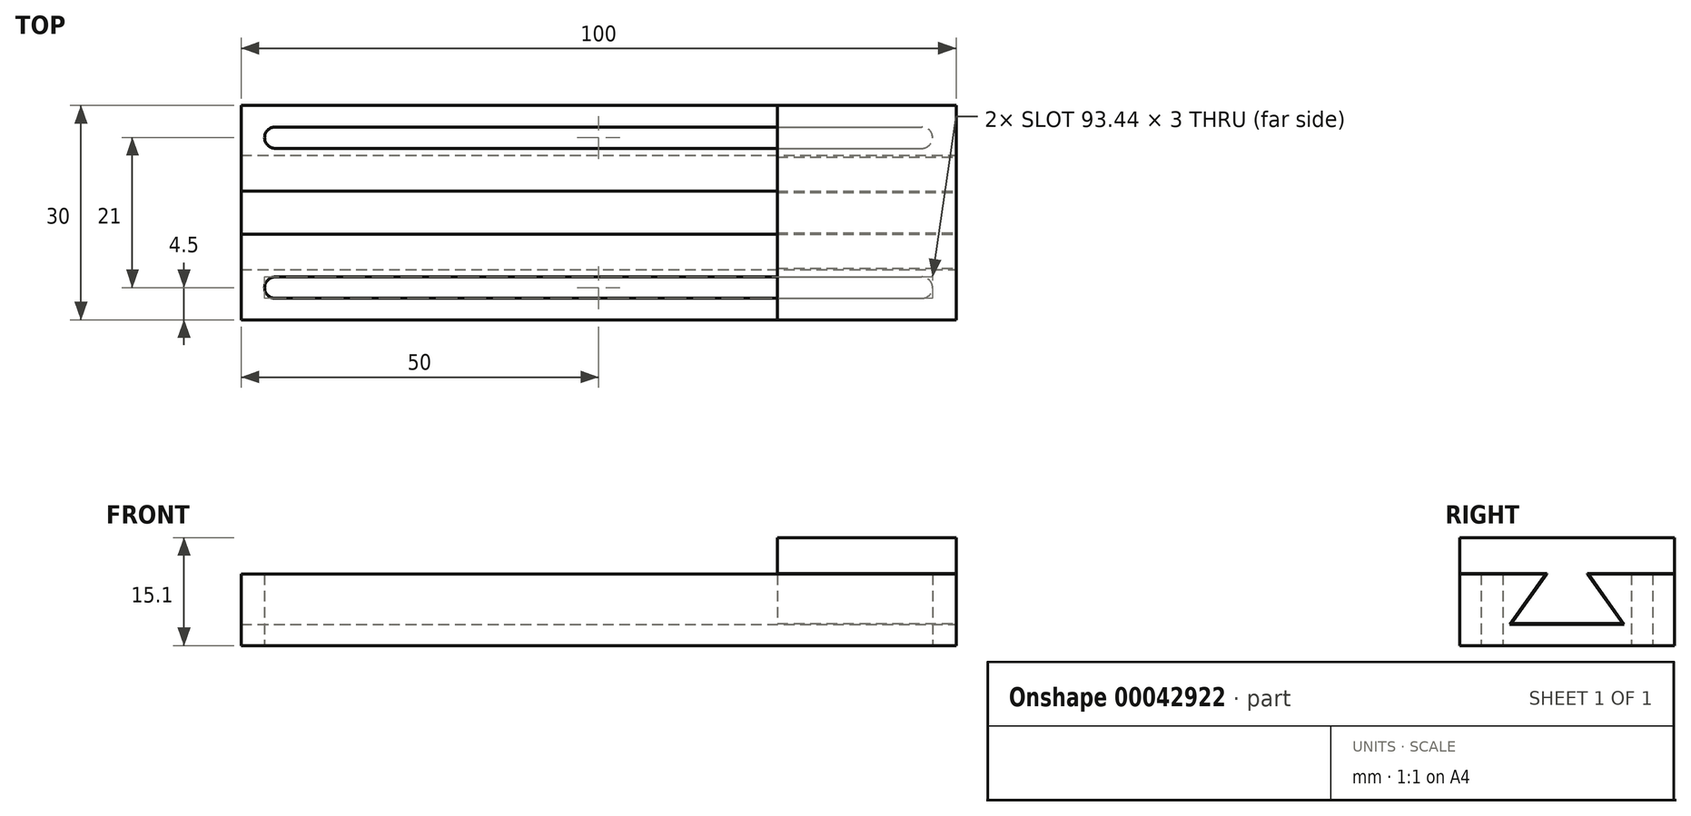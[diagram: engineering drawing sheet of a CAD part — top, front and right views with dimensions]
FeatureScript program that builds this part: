
annotation { "Feature Type Name" : "Feature", "Feature Type Description" : "" }
export const myFeature = defineFeature(function(context is Context, id is Id, definition is map)
    precondition{}
    {
        {
            var Q0;
            Q0=qCreatedBy(makeId("Top.planeOp"),FACE);
            var sketch = newSketch(context, id + "F0", { "sketchPlane" : qUnion([Q0])});
            skLineSegment(sketch, "E0.bottom", {"start": v(-50, 15) * mm, "end": v(50, 15) * mm});
            skLineSegment(sketch, "E0.top", {"start": v(-50, -15) * mm, "end": v(50, -15) * mm});
            skLineSegment(sketch, "E0.left", {"start": v(-50, 15) * mm, "end": v(-50, -15) * mm});
            skLineSegment(sketch, "E0.right", {"start": v(50, 15) * mm, "end": v(50, -15) * mm});
            skLineSegment(sketch, "E1", {"start": v(0, 15) * mm, "end": v(0, -15) * mm, "construction": true});
            skLineSegment(sketch, "E2", {"start": v(-50, 0) * mm, "end": v(50, 0) * mm, "construction": true});
            skLineSegment(sketch, "E3", {"start": v(-50, 3) * mm, "end": v(50, 3) * mm});
            skLineSegment(sketch, "E4", {"start": v(-50, -3) * mm, "end": v(50, -3) * mm});
            skLineSegment(sketch, "E5", {"start": v(-50, 6) * mm, "end": v(50, 6) * mm});
            skLineSegment(sketch, "E6", {"start": v(50, 6) * mm, "end": v(50, -6) * mm});
            skLineSegment(sketch, "E7", {"start": v(50, -6) * mm, "end": v(-50, -6) * mm});
            skLineSegment(sketch, "E8.bottom", {"start": v(-45.22, -9) * mm, "end": v(45.22, -9) * mm});
            skLineSegment(sketch, "E8.top", {"start": v(-45.22, -12) * mm, "end": v(45.22, -12) * mm});
            skLineSegment(sketch, "E8.left", {"start": v(-45.22, -9) * mm, "end": v(-45.22, -12) * mm});
            skLineSegment(sketch, "E8.right", {"start": v(45.22, -9) * mm, "end": v(45.22, -12) * mm});
            skLineSegment(sketch, "E9.bottom", {"start": v(-45.22, 12) * mm, "end": v(45.22, 12) * mm});
            skLineSegment(sketch, "E9.top", {"start": v(-45.22, 9) * mm, "end": v(45.22, 9) * mm});
            skLineSegment(sketch, "E9.left", {"start": v(-45.22, 12) * mm, "end": v(-45.22, 9) * mm});
            skLineSegment(sketch, "E9.right", {"start": v(45.22, 12) * mm, "end": v(45.22, 9) * mm});
            skLineSegment(sketch, "E10", {"start": v(0, -12) * mm, "end": v(0, -15) * mm, "construction": true});
            skLineSegment(sketch, "E11", {"start": v(0, 15) * mm, "end": v(0, 12) * mm, "construction": true});
            skLineSegment(sketch, "E12", {"start": v(0, -6) * mm, "end": v(0, -15) * mm, "construction": true});
            skLineSegment(sketch, "E13", {"start": v(0, 15) * mm, "end": v(0, 6) * mm, "construction": true});
            skPoint(sketch, "E14", {"position": v(0, 10.5) * mm});
            skPoint(sketch, "E15", {"position": v(-45.22, 10.5) * mm});
            skPoint(sketch, "E16", {"position": v(-45.22, -10.5) * mm});
            skPoint(sketch, "E17", {"position": v(45.22, -10.5) * mm});
            skPoint(sketch, "E18", {"position": v(45.22, 10.5) * mm});
            skLineSegment(sketch, "E19", {"start": v(-50, 72.94) * mm, "end": v(-50, -39.34) * mm, "construction": true});
            skLineSegment(sketch, "E20", {"start": v(0, -31.19) * mm, "end": v(0, 115.5) * mm, "construction": true});
            skSolve(sketch);
        }
        {
            var Q0;
            {var subQ0=sQuery(id+"F0.wireOp",EDGE,"E0.bottom");Q0=makeQuery(id+"F0.imprint","IMPRINT",FACE,{"disambiguationData":[TD([[makeQuery(id+"F0.imprint","IMPRINT",EDGE,{"derivedFrom":subQ0}),-1.0]])]});}
            var Q1;
            {var subQ2=sQuery(id+"F0.wireOp",EDGE,"E3");Q1=makeQuery(id+"F0.imprint","IMPRINT",FACE,{"disambiguationData":[TD([[makeQuery(id+"F0.imprint","IMPRINT",EDGE,{"derivedFrom":subQ2}),1.0]])]});}
            var Q2;
            {var subQ2=sQuery(id+"F0.wireOp",EDGE,"E0.top");Q2=makeQuery(id+"F0.imprint","IMPRINT",FACE,{"disambiguationData":[TD([[makeQuery(id+"F0.imprint","IMPRINT",EDGE,{"derivedFrom":subQ2}),1.0]])]});}
            var Q3;
            {var subQ2=sQuery(id+"F0.wireOp",EDGE,"E4");Q3=makeQuery(id+"F0.imprint","IMPRINT",FACE,{"disambiguationData":[TD([[makeQuery(id+"F0.imprint","IMPRINT",EDGE,{"derivedFrom":subQ2}),-1.0]])]});}
            extrude(context, id + "F1", {"entities" : qUnion([Q0, Q1, Q2, Q3]), "depth" : 10 * mm});
        }
        {
            var Q0;
            {var subQ2=sQuery(id+"F0.wireOp",EDGE,"E3");Q0=makeQuery(id+"F0.imprint","IMPRINT",FACE,{"disambiguationData":[TD([[makeQuery(id+"F0.imprint","IMPRINT",EDGE,{"derivedFrom":subQ2}),-1.0]])]});}
            extrude(context, id + "F2", {"entities" : qUnion([Q0]), "operationType" : NewBodyOperationType.ADD, "depth" : 3 * mm});
        }
        {
            var Q0;
            Q0=sQuery(id+"F0.wireOp",VERTEX,"E16");
            var Q1;
            Q1=sQuery(id+"F0.wireOp",VERTEX,"E17");
            var Q2;
            Q2=sQuery(id+"F0.wireOp",VERTEX,"E15");
            var Q3;
            Q3=sQuery(id+"F0.wireOp",VERTEX,"E18");
            var Q4;
            Q4=makeQuery(id+"F1.opExtrude","SWEPT_BODY",BODY,{"disambiguationData":[OSD([sQuery(id+"F0.wireOp",EDGE,"E0.top"),sQuery(id+"F0.wireOp",EDGE,"E0.left"),sQuery(id+"F0.wireOp",EDGE,"E0.right"),sQuery(id+"F0.wireOp",EDGE,"E4"),sQuery(id+"F0.wireOp",EDGE,"E6"),sQuery(id+"F0.wireOp",EDGE,"E8.bottom"),sQuery(id+"F0.wireOp",EDGE,"E8.top"),sQuery(id+"F0.wireOp",EDGE,"E8.left"),sQuery(id+"F0.wireOp",EDGE,"E8.right")])]});
            var Q5;
            Q5=makeQuery(id+"F1.opExtrude","SWEPT_BODY",BODY,{"disambiguationData":[OSD([sQuery(id+"F0.wireOp",EDGE,"E0.bottom"),sQuery(id+"F0.wireOp",EDGE,"E0.left"),sQuery(id+"F0.wireOp",EDGE,"E0.right"),sQuery(id+"F0.wireOp",EDGE,"E3"),sQuery(id+"F0.wireOp",EDGE,"E6"),sQuery(id+"F0.wireOp",EDGE,"E9.bottom"),sQuery(id+"F0.wireOp",EDGE,"E9.top"),sQuery(id+"F0.wireOp",EDGE,"E9.left"),sQuery(id+"F0.wireOp",EDGE,"E9.right")])]});
            hole(context, id + "F3", {"style" : HoleStyle.SIMPLE, "holeDiameter" : 3 * mm, "endStyle" : HoleEndStyle.BLIND, "oppositeDirection" : true, "holeDepth" : 20 * mm, "locations" : qUnion([Q0, Q1, Q2, Q3]), "scope" : qUnion([Q4, Q5]), "startFromSketch" : true});
        }
        {
            var Q0;
            {var subQ0=sQuery(id+"F0.wireOp",EDGE,"E6");var subQ1=sQuery(id+"F0.wireOp",EDGE,"E0.right");Q0=makeQuery(id+"Fmz5GTSr20wqwjv_3.boolean.opBoolean","MERGE",FACE,{"derivedFrom":[makeQuery(id+"F1.opExtrude","SWEPT_FACE",FACE,{"disambiguationData":[OSD([subQ1,subQ0]),TDD([makeQuery(id+"F0.imprint","IMPRINT",EDGE,{"disambiguationData":[TD([[makeQuery(id+"F0.imprint","INTERSECT",VERTEX,{"derivedFrom":[sQuery(id+"F0.wireOp",EDGE,"E0.bottom"),subQ1]}),-1.0]])],"derivedFrom":subQ1}),makeQuery(id+"F0.imprint","IMPRINT",EDGE,{"disambiguationData":[TD([[makeQuery(id+"F0.imprint","INTERSECT",VERTEX,{"derivedFrom":[sQuery(id+"F0.wireOp",EDGE,"E3"),subQ0]}),1.0]])],"derivedFrom":subQ0})])]}),makeQuery(id+"F1.opExtrude","SWEPT_FACE",FACE,{"disambiguationData":[OSD([subQ1,subQ0]),TDD([makeQuery(id+"F0.imprint","IMPRINT",EDGE,{"disambiguationData":[TD([[makeQuery(id+"F0.imprint","INTERSECT",VERTEX,{"derivedFrom":[sQuery(id+"F0.wireOp",EDGE,"E0.top"),subQ1]}),1.0]])],"derivedFrom":subQ1}),makeQuery(id+"F0.imprint","IMPRINT",EDGE,{"disambiguationData":[TD([[makeQuery(id+"F0.imprint","INTERSECT",VERTEX,{"derivedFrom":[sQuery(id+"F0.wireOp",EDGE,"E4"),subQ0]}),-1.0]])],"derivedFrom":subQ0})])]}),makeQuery(id+"F2.opExtrude","SWEPT_FACE",FACE,{"disambiguationData":[OSD([subQ0])]})]});}
            var sketch = newSketch(context, id + "F4", { "sketchPlane" : qUnion([Q0])});
            skLineSegment(sketch, "E21", {"start": v(3, 3) * mm, "end": v(8, 3) * mm});
            skLineSegment(sketch, "E22", {"start": v(8, 3) * mm, "end": v(3, 10) * mm});
            skLineSegment(sketch, "E23", {"start": v(-3, 3) * mm, "end": v(-8, 3) * mm});
            skLineSegment(sketch, "E24", {"start": v(-8, 3) * mm, "end": v(-3, 10) * mm});
            skLineSegment(sketch, "E25", {"start": v(3, 10) * mm, "end": v(3, 3) * mm});
            skLineSegment(sketch, "E26", {"start": v(-3, 10) * mm, "end": v(-3, 3) * mm});
            skLineSegment(sketch, "E27", {"start": v(-7.76, 3.12) * mm, "end": v(7.76, 3.13) * mm});
            skLineSegment(sketch, "E28", {"start": v(7.76, 3.13) * mm, "end": v(2.85, 10) * mm});
            skLineSegment(sketch, "E29", {"start": v(2.85, 10) * mm, "end": v(2.85, 10.1) * mm});
            skLineSegment(sketch, "E30", {"start": v(2.85, 10.1) * mm, "end": v(15, 10.1) * mm});
            skLineSegment(sketch, "E31", {"start": v(15, 10.1) * mm, "end": v(15, 15.1) * mm});
            skLineSegment(sketch, "E32", {"start": v(15, 15.1) * mm, "end": v(-15, 15.1) * mm});
            skLineSegment(sketch, "E33", {"start": v(-15, 15.1) * mm, "end": v(-15, 10.1) * mm});
            skLineSegment(sketch, "E34", {"start": v(-15, 10.1) * mm, "end": v(-2.85, 10.1) * mm});
            skLineSegment(sketch, "E35", {"start": v(-2.85, 10.1) * mm, "end": v(-2.85, 10) * mm});
            skLineSegment(sketch, "E36", {"start": v(-2.85, 10) * mm, "end": v(-7.76, 3.12) * mm});
            skSolve(sketch);
        }
        {
            var Q0;
            Q0=makeQuery(id+"F4.imprint","IMPRINT",FACE,{"disambiguationData":[TD([[makeQuery(id+"F4.imprint","IMPRINT",EDGE,{"derivedFrom":sQuery(id+"F4.wireOp",EDGE,"E23")}),-1.0]])]});
            var Q1;
            Q1=makeQuery(id+"F4.imprint","IMPRINT",FACE,{"disambiguationData":[TD([[makeQuery(id+"F4.imprint","IMPRINT",EDGE,{"derivedFrom":sQuery(id+"F4.wireOp",EDGE,"E21")}),1.0]])]});
            var Q2;
            {var subQ0=sQuery(id+"F4.wireOp",EDGE,"E36");var subQ1=sQuery(id+"F4.wireOp",EDGE,"E26");var subQ2=makeQuery(id+"F4.imprint","INTERSECT",VERTEX,{"derivedFrom":[subQ1,subQ0]});Q2=makeQuery(id+"F4.imprint","IMPRINT",FACE,{"disambiguationData":[TD([[makeQuery(id+"F4.imprint","IMPRINT",EDGE,{"disambiguationData":[TD([[subQ2,-1.0]])],"derivedFrom":subQ1}),-1.0]])]});}
            var Q3;
            {var subQ7=sQuery(id+"F4.wireOp",EDGE,"E29");Q3=makeQuery(id+"F4.imprint","IMPRINT",FACE,{"disambiguationData":[TD([[makeQuery(id+"F4.imprint","IMPRINT",EDGE,{"derivedFrom":subQ7}),1.0]])]});}
            var Q4;
            {var subQ0=sQuery(id+"F4.wireOp",EDGE,"E28");var subQ1=sQuery(id+"F4.wireOp",EDGE,"E25");var subQ2=makeQuery(id+"F4.imprint","INTERSECT",VERTEX,{"derivedFrom":[subQ1,subQ0]});Q4=makeQuery(id+"F4.imprint","IMPRINT",FACE,{"disambiguationData":[TD([[makeQuery(id+"F4.imprint","IMPRINT",EDGE,{"disambiguationData":[TD([[subQ2,-1.0]])],"derivedFrom":subQ1}),1.0]])]});}
            extrude(context, id + "F5", {"entities" : qUnion([Q0, Q1, Q2, Q3, Q4]), "operationType" : NewBodyOperationType.REMOVE, "endBound" : BoundingType.THROUGH_ALL, "oppositeDirection" : true, "depth" : 25 * mm});
        }
        {
            var Q0;
            {var subQ7=sQuery(id+"F4.wireOp",EDGE,"E29");Q0=makeQuery(id+"F4.imprint","IMPRINT",FACE,{"disambiguationData":[TD([[makeQuery(id+"F4.imprint","IMPRINT",EDGE,{"derivedFrom":subQ7}),1.0]])]});}
            var Q1;
            {var subQ0=sQuery(id+"F4.wireOp",EDGE,"E36");var subQ1=sQuery(id+"F4.wireOp",EDGE,"E26");var subQ2=makeQuery(id+"F4.imprint","INTERSECT",VERTEX,{"derivedFrom":[subQ1,subQ0]});Q1=makeQuery(id+"F4.imprint","IMPRINT",FACE,{"disambiguationData":[TD([[makeQuery(id+"F4.imprint","IMPRINT",EDGE,{"disambiguationData":[TD([[subQ2,-1.0]])],"derivedFrom":subQ1}),-1.0]])]});}
            var Q2;
            {var subQ0=sQuery(id+"F4.wireOp",EDGE,"E28");var subQ1=sQuery(id+"F4.wireOp",EDGE,"E25");var subQ2=makeQuery(id+"F4.imprint","INTERSECT",VERTEX,{"derivedFrom":[subQ1,subQ0]});Q2=makeQuery(id+"F4.imprint","IMPRINT",FACE,{"disambiguationData":[TD([[makeQuery(id+"F4.imprint","IMPRINT",EDGE,{"disambiguationData":[TD([[subQ2,-1.0]])],"derivedFrom":subQ1}),1.0]])]});}
            extrude(context, id + "F6", {"entities" : qUnion([Q0, Q1, Q2]), "oppositeDirection" : true, "depth" : 25 * mm});
        }
    });
